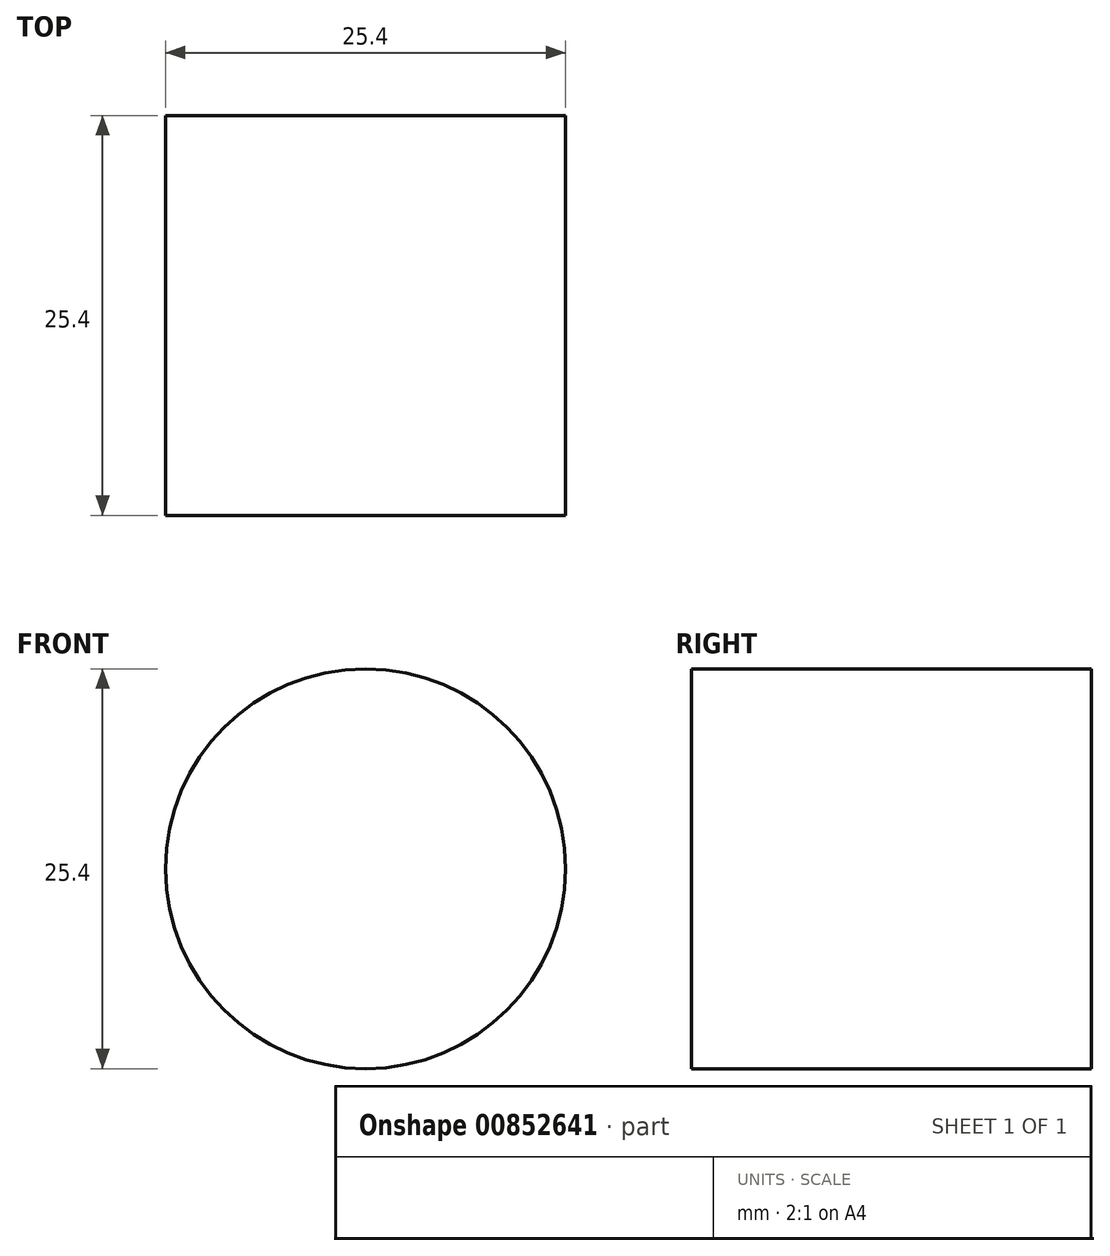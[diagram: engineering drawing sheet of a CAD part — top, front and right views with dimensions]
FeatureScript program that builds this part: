
annotation { "Feature Type Name" : "Feature", "Feature Type Description" : "" }
export const myFeature = defineFeature(function(context is Context, id is Id, definition is map)
    precondition{}
    {
        {
            var Q0;
            Q0=qCreatedBy(makeId("Front.planeOp"),FACE);
            var sketch = newSketch(context, id + "F0", { "sketchPlane" : qUnion([Q0])});
            skCircle(sketch, "E0", {"center": v(0, 0) * mm, "radius": 12.7 * mm});
            skSolve(sketch);
        }
        {
            var Q0;
            Q0 = qSketchRegion(id + "F0", true);
            extrude(context, id + "F1", {"entities" : qUnion([Q0]), "endBound" : BoundingType.SYMMETRIC, "depth" : 25.4 * mm, "offsetDistance" : 25.4 * mm});
        }
    });
